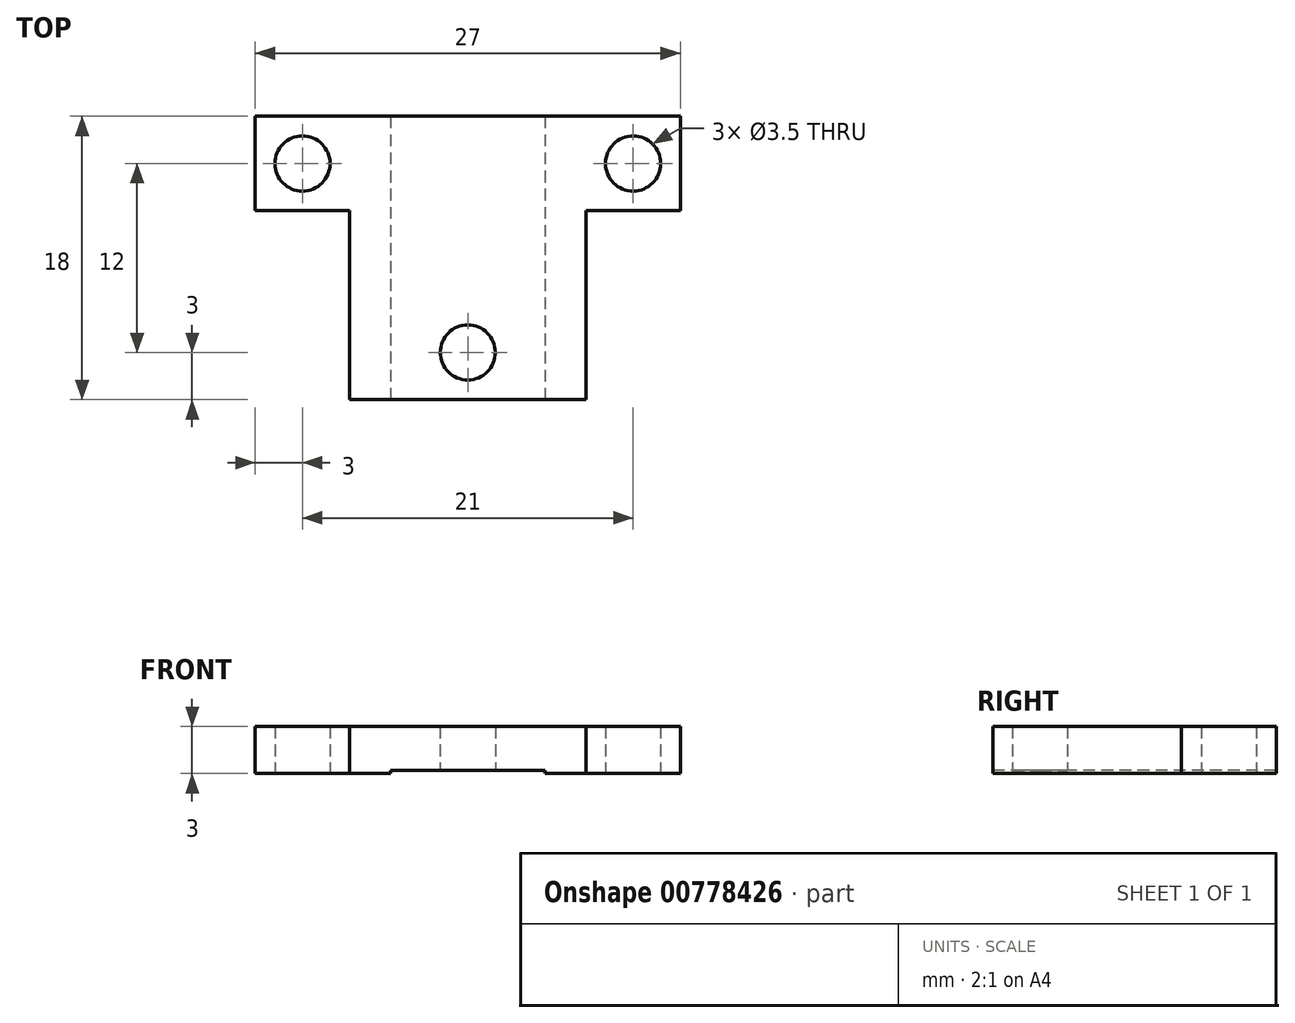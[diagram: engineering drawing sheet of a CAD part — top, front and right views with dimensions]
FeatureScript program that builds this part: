
annotation { "Feature Type Name" : "Feature", "Feature Type Description" : "" }
export const myFeature = defineFeature(function(context is Context, id is Id, definition is map)
    precondition{}
    {
        {
            var Q0;
            Q0=qCreatedBy(makeId("Top.planeOp"),FACE);
            var sketch = newSketch(context, id + "F0", { "sketchPlane" : qUnion([Q0])});
            skLineSegment(sketch, "E0.bottom", {"start": v(-7.5, 9) * mm, "end": v(7.5, 9) * mm});
            skLineSegment(sketch, "E0.top", {"start": v(-7.5, -9) * mm, "end": v(7.5, -9) * mm});
            skLineSegment(sketch, "E0.left", {"start": v(-7.5, 9) * mm, "end": v(-7.5, -9) * mm});
            skLineSegment(sketch, "E0.right", {"start": v(7.5, 9) * mm, "end": v(7.5, -9) * mm});
            skPoint(sketch, "E0.middle", {"position": v(0, 0) * mm});
            skLineSegment(sketch, "E1.bottom", {"start": v(-7.5, 9) * mm, "end": v(-13.5, 9) * mm});
            skLineSegment(sketch, "E1.top", {"start": v(-7.5, 3) * mm, "end": v(-13.5, 3) * mm});
            skLineSegment(sketch, "E1.left", {"start": v(-7.5, 9) * mm, "end": v(-7.5, 3) * mm});
            skLineSegment(sketch, "E1.right", {"start": v(-13.5, 9) * mm, "end": v(-13.5, 3) * mm});
            skLineSegment(sketch, "E2.MirrorCS", {"start": v(7.5, 3) * mm, "end": v(13.5, 3) * mm});
            skLineSegment(sketch, "E3.MirrorCS", {"start": v(13.5, 9) * mm, "end": v(13.5, 3) * mm});
            skLineSegment(sketch, "E4.MirrorCS", {"start": v(7.5, 9) * mm, "end": v(13.5, 9) * mm});
            skLineSegment(sketch, "E5", {"start": v(-10.5, 3) * mm, "end": v(-10.5, 6) * mm});
            skCircle(sketch, "E6", {"center": v(-10.5, 6) * mm, "radius": 1.75 * mm});
            skCircle(sketch, "E7.MirrorC", {"center": v(10.5, 6) * mm, "radius": 1.75 * mm});
            skLineSegment(sketch, "E8", {"start": v(0, -9) * mm, "end": v(0, -6) * mm});
            skCircle(sketch, "E9", {"center": v(0, -6) * mm, "radius": 1.75 * mm});
            skSolve(sketch);
        }
        {
            var Q0;
            {var subQ1=sQuery(id+"F0.wireOp",EDGE,"E0.bottom");Q0=makeQuery(id+"F0.imprint","IMPRINT",FACE,{"disambiguationData":[TD([[makeQuery(id+"F0.imprint","IMPRINT",EDGE,{"derivedFrom":subQ1}),-1.0]])]});}
            var sketch = newSketch(context, id + "F1", { "sketchPlane" : qUnion([Q0])});
            skLineSegment(sketch, "E10.bottom", {"start": v(-4.9, 9) * mm, "end": v(4.9, 9) * mm});
            skLineSegment(sketch, "E10.top", {"start": v(-4.9, -9) * mm, "end": v(4.9, -9) * mm});
            skLineSegment(sketch, "E10.left", {"start": v(-4.9, 9) * mm, "end": v(-4.9, -9) * mm});
            skLineSegment(sketch, "E10.right", {"start": v(4.9, 9) * mm, "end": v(4.9, -9) * mm});
            skPoint(sketch, "E10.middle", {"position": v(0, 0) * mm});
            skSolve(sketch);
        }
        {
            var Q0;
            Q0 = qSketchRegion(id + "F0", true);
            extrude(context, id + "F2", {"entities" : qUnion([Q0]), "depth" : 3 * mm, "offsetDistance" : 25 * mm});
        }
        {
            var Q0;
            Q0 = qSketchRegion(id + "F1", true);
            extrude(context, id + "F3", {"entities" : qUnion([Q0]), "operationType" : NewBodyOperationType.REMOVE, "oppositeDirection" : true, "depth" : -.2 * mm, "offsetDistance" : 25 * mm});
        }
    });
